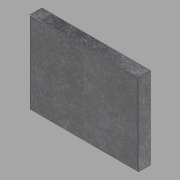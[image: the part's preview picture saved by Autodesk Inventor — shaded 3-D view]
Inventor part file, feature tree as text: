
AUTODESK INVENTOR PART (.ipt)
format: ipt  version: 2022.1 (Build 261234020, 234B)  size: 109,568 bytes
history: native  units: in
note: dims shown in document units (in); Inventor stores cm internally (conversion verified against a paired STEP export)
features: extrude x1, fillet x1, sketch x1
ambient origin geometry x8: Origin, YZ Plane, XZ Plane, XY Plane, X Axis, Y Axis, Z Axis, Center Point
bodies: Solid1 (feature_tree)
feature tree (3):
  extrude  "Extrusion1"  Depth=40.0in
  fillet  "Fillet1"  Radius=6.0in
  sketch  "Sketch1"  dims[d0=53.0in d1=40.0in d2=6.0in d3=0.0in d4=0.25in]
